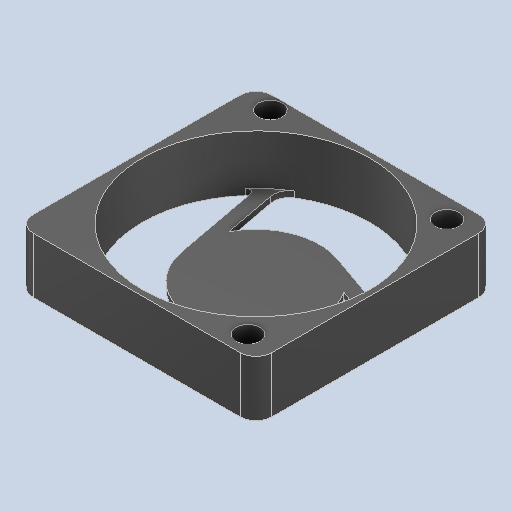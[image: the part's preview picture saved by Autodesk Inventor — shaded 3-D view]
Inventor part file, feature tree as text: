
AUTODESK INVENTOR PART (.ipt)
format: ipt  version: 2024.3 (Build 283343000, 343)  size: 137,216 bytes
history: native  units: in
note: dims shown in document units (in); Inventor stores cm internally (conversion verified against a paired STEP export)
features: fillet x1
ambient origin geometry x8: Origin, YZ Plane, XZ Plane, XY Plane, X Axis, Y Axis, Z Axis, Center Point
bodies: Solid1 (feature_tree)
feature tree (1):
  fillet  "Fillet2"  [1 undecoded]
note: 1 required parameter value undecoded (feature->parameter linkage not recoverable at this tier; creation-order binding heuristic only, values carry confidence <= 0.55)
